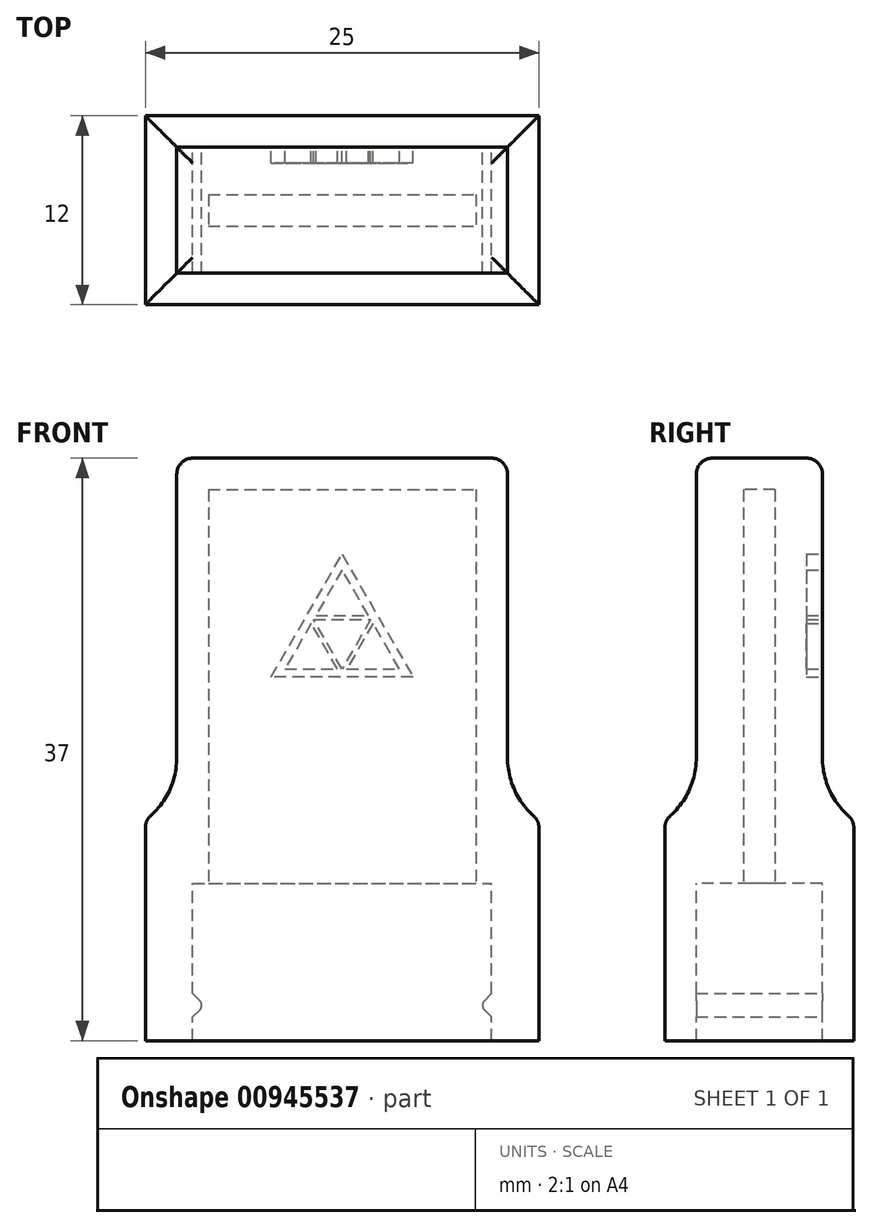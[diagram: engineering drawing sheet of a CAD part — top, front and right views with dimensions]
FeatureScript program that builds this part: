
annotation { "Feature Type Name" : "Feature", "Feature Type Description" : "" }
export const myFeature = defineFeature(function(context is Context, id is Id, definition is map)
    precondition{}
    {
        {
            var Q0;
            Q0=qCreatedBy(makeId("Top.planeOp"),FACE);
            var sketch = newSketch(context, id + "F0", { "sketchPlane" : qUnion([Q0])});
            skLineSegment(sketch, "E0.bottom", {"start": v(0, 0) * mm, "end": v(25, 0) * mm});
            skLineSegment(sketch, "E0.top", {"start": v(0, 12) * mm, "end": v(25, 12) * mm});
            skLineSegment(sketch, "E0.left", {"start": v(0, 0) * mm, "end": v(0, 12) * mm});
            skLineSegment(sketch, "E0.right", {"start": v(25, 0) * mm, "end": v(25, 12) * mm});
            skLineSegment(sketch, "E1.bottom", {"start": v(3, 10) * mm, "end": v(22, 10) * mm});
            skLineSegment(sketch, "E1.top", {"start": v(3, 2) * mm, "end": v(22, 2) * mm});
            skLineSegment(sketch, "E1.left", {"start": v(3, 10) * mm, "end": v(3, 2) * mm});
            skLineSegment(sketch, "E1.right", {"start": v(22, 10) * mm, "end": v(22, 2) * mm});
            skSolve(sketch);
        }
        {
            var Q0;
            Q0=makeQuery(id+"F0.imprint","IMPRINT",FACE,{"disambiguationData":[TD([[makeQuery(id+"F0.imprint","IMPRINT",EDGE,{"derivedFrom":sQuery(id+"F0.wireOp",EDGE,"E0.bottom")}),1.0]])]});
            extrude(context, id + "F1", {"entities" : qUnion([Q0]), "oppositeDirection" : true, "depth" : 10 * mm, "offsetDistance" : 25 * mm});
        }
        {
            var Q0;
            Q0=qCreatedBy(makeId("Top.planeOp"),FACE);
            var sketch = newSketch(context, id + "F2", { "sketchPlane" : qUnion([Q0])});
            skLineSegment(sketch, "E2.bottom", {"start": v(4, 7) * mm, "end": v(21, 7) * mm});
            skLineSegment(sketch, "E2.top", {"start": v(4, 5) * mm, "end": v(21, 5) * mm});
            skLineSegment(sketch, "E2.left", {"start": v(4, 7) * mm, "end": v(4, 5) * mm});
            skLineSegment(sketch, "E2.right", {"start": v(21, 7) * mm, "end": v(21, 5) * mm});
            skLineSegment(sketch, "E3.bottom", {"start": v(2, 10) * mm, "end": v(23, 10) * mm});
            skLineSegment(sketch, "E3.top", {"start": v(2, 2) * mm, "end": v(23, 2) * mm});
            skLineSegment(sketch, "E3.left", {"start": v(2, 10) * mm, "end": v(2, 2) * mm});
            skLineSegment(sketch, "E3.right", {"start": v(23, 10) * mm, "end": v(23, 2) * mm});
            skSolve(sketch);
        }
        {
            var Q0;
            Q0=makeQuery(id+"F2.imprint","IMPRINT",FACE,{"disambiguationData":[TD([[makeQuery(id+"F2.imprint","IMPRINT",EDGE,{"derivedFrom":sQuery(id+"F2.wireOp",EDGE,"E2.bottom")}),1.0]])]});
            extrude(context, id + "F3", {"entities" : qUnion([Q0]), "depth" : 25 * mm, "offsetDistance" : 25 * mm});
        }
        {
            var Q0;
            Q0=makeQuery(id+"F3.opExtrude","CAP_FACE",FACE,{"disambiguationData":[OSD([sQuery(id+"F2.wireOp",EDGE,"E2.bottom"),sQuery(id+"F2.wireOp",EDGE,"E2.top"),sQuery(id+"F2.wireOp",EDGE,"E2.left"),sQuery(id+"F2.wireOp",EDGE,"E2.right"),sQuery(id+"F2.wireOp",EDGE,"E3.bottom"),sQuery(id+"F2.wireOp",EDGE,"E3.top"),sQuery(id+"F2.wireOp",EDGE,"E3.left"),sQuery(id+"F2.wireOp",EDGE,"E3.right")])],"isStart":false});
            var sketch = newSketch(context, id + "F4", { "sketchPlane" : qUnion([Q0])});
            skSolve(sketch);
        }
        {
            var Q0;
            Q0=makeQuery(id+"F4.imprint","IMPRINT",FACE,{"disambiguationData":[TD([[makeQuery(id+"F4.imprint","IMPRINT",EDGE,{"derivedFrom":makeQuery(id+"F3.opExtrude","CAP_EDGE",EDGE,{"disambiguationData":[OSD([sQuery(id+"F2.wireOp",EDGE,"E2.bottom")])],"isStart":false})}),1.0]])]});
            var Q1;
            Q1=makeQuery(id+"F4.imprint","IMPRINT",FACE,{"disambiguationData":[TD([[makeQuery(id+"F4.imprint","IMPRINT",EDGE,{"derivedFrom":makeQuery(id+"F3.opExtrude","CAP_EDGE",EDGE,{"disambiguationData":[OSD([sQuery(id+"F2.wireOp",EDGE,"E2.bottom")])],"isStart":false})}),-1.0]])]});
            extrude(context, id + "F5", {"entities" : qUnion([Q0, Q1]), "operationType" : NewBodyOperationType.ADD, "depth" : 2 * mm, "offsetDistance" : 25 * mm});
        }
        {
            var Q0;
            Q0=makeQuery(id+"F1.opExtrude","CAP_FACE",FACE,{"disambiguationData":[OSD([sQuery(id+"F0.wireOp",EDGE,"E0.bottom"),sQuery(id+"F0.wireOp",EDGE,"E0.top"),sQuery(id+"F0.wireOp",EDGE,"E0.left"),sQuery(id+"F0.wireOp",EDGE,"E0.right"),sQuery(id+"F0.wireOp",EDGE,"E1.bottom"),sQuery(id+"F0.wireOp",EDGE,"E1.top"),sQuery(id+"F0.wireOp",EDGE,"E1.left"),sQuery(id+"F0.wireOp",EDGE,"E1.right")])],"isStart":true});
            var sketch = newSketch(context, id + "F6", { "sketchPlane" : qUnion([Q0])});
            skSolve(sketch);
        }
        {
            var Q0;
            Q0=makeQuery(id+"F6.imprint","IMPRINT",FACE,{"disambiguationData":[TD([[makeQuery(id+"F6.imprint","IMPRINT",EDGE,{"derivedFrom":makeQuery(id+"F1.opExtrude","CAP_EDGE",EDGE,{"disambiguationData":[OSD([sQuery(id+"F0.wireOp",EDGE,"E0.bottom")])],"isStart":true})}),1.0]])]});
            extrude(context, id + "F7", {"entities" : qUnion([Q0]), "operationType" : NewBodyOperationType.ADD, "depth" : 4 * mm, "offsetDistance" : 25 * mm});
        }
        {
            var Q0;
            Q0=qCreatedBy(makeId("Front.planeOp"),FACE);
            cPlane(context, id + "F8", {"entities" : qUnion([Q0]), "cplaneType" : CPlaneType.OFFSET, "offset" : 6 * mm, "oppositeDirection" : true, "width" : 150 * mm, "height" : 150 * mm});
        }
        {
            var Q0;
            Q0=qCreatedBy(id+"F8.planeOp",FACE);
            var sketch = newSketch(context, id + "F9", { "sketchPlane" : qUnion([Q0])});
            skLineSegment(sketch, "E4", {"start": v(0, 0) * mm, "end": v(0, -10) * mm});
            skLineSegment(sketch, "E5", {"start": v(0, -10) * mm, "end": v(3, -10) * mm});
            skLineSegment(sketch, "E6", {"start": v(3, -10) * mm, "end": v(3, -8.5) * mm});
            skLineSegment(sketch, "E7", {"start": v(3, -8.5) * mm, "end": v(3.47, -8.03) * mm});
            skLineSegment(sketch, "E8", {"start": v(3.47, -7.47) * mm, "end": v(3, -7) * mm});
            skLineSegment(sketch, "E9", {"start": v(3, -7) * mm, "end": v(3, -8.5) * mm});
            skPoint(sketch, "E10.visualSharp", {"position": v(3.75, -7.75) * mm});
            skArc(sketch, "E10.filletArc", {"start": v(3.47, -8.03) * mm, "mid": v(3.58, -7.75) * mm, "end": v(3.47, -7.47) * mm});
            skLineSegment(sketch, "E11", {"start": v(22, -8.5) * mm, "end": v(22, -7) * mm});
            skLineSegment(sketch, "E12", {"start": v(22, -7) * mm, "end": v(21.53, -7.47) * mm});
            skLineSegment(sketch, "E13", {"start": v(21.53, -8.03) * mm, "end": v(22, -8.5) * mm});
            skPoint(sketch, "E14.visualSharp", {"position": v(21.25, -7.75) * mm});
            skArc(sketch, "E14.filletArc", {"start": v(21.53, -7.47) * mm, "mid": v(21.42, -7.75) * mm, "end": v(21.53, -8.03) * mm});
            skSolve(sketch);
        }
        {
            var Q0;
            Q0=makeQuery(id+"F9.imprint","IMPRINT",FACE,{"disambiguationData":[TD([[makeQuery(id+"F9.imprint","IMPRINT",EDGE,{"derivedFrom":sQuery(id+"F9.wireOp",EDGE,"E7")}),1.0]])]});
            var Q1;
            Q1=makeQuery(id+"F9.imprint","IMPRINT",FACE,{"disambiguationData":[TD([[makeQuery(id+"F9.imprint","IMPRINT",EDGE,{"derivedFrom":sQuery(id+"F9.wireOp",EDGE,"E11")}),1.0]])]});
            extrude(context, id + "F10", {"entities" : qUnion([Q0, Q1]), "operationType" : NewBodyOperationType.ADD, "endBound" : BoundingType.UP_TO_NEXT, "depth" : 25 * mm, "offsetDistance" : 25 * mm, "hasSecondDirection" : true, "secondDirectionBound" : SecondDirectionBoundingType.UP_TO_NEXT, "secondDirectionOppositeDirection" : true, "secondDirectionDepth" : 25 * mm});
        }
        {
            var Q0;
            {var subQ0=sQuery(id+"F2.wireOp",EDGE,"E3.top");Q0=makeQuery(id+"F7.boolean.opBoolean","INTERSECT",EDGE,{"derivedFrom":[makeQuery(id+"F5.boolean.opBoolean","MERGE",FACE,{"derivedFrom":[makeQuery(id+"F3.opExtrude","SWEPT_FACE",FACE,{"disambiguationData":[OSD([subQ0])]}),makeQuery(id+"F5.opExtrude","SWEPT_FACE",FACE,{"disambiguationData":[OSD([subQ0])]})]}),makeQuery(id+"F7.opExtrude","CAP_FACE",FACE,{"disambiguationData":[OSD([sQuery(id+"F0.wireOp",EDGE,"E0.bottom"),sQuery(id+"F0.wireOp",EDGE,"E0.top"),sQuery(id+"F0.wireOp",EDGE,"E0.left"),sQuery(id+"F0.wireOp",EDGE,"E0.right"),sQuery(id+"F0.wireOp",EDGE,"E1.bottom"),sQuery(id+"F0.wireOp",EDGE,"E1.top"),sQuery(id+"F0.wireOp",EDGE,"E1.left"),sQuery(id+"F0.wireOp",EDGE,"E1.right")])],"isStart":false})]});}
            var Q1;
            {var subQ0=sQuery(id+"F2.wireOp",EDGE,"E3.right");Q1=makeQuery(id+"F7.boolean.opBoolean","INTERSECT",EDGE,{"derivedFrom":[makeQuery(id+"F5.boolean.opBoolean","MERGE",FACE,{"derivedFrom":[makeQuery(id+"F3.opExtrude","SWEPT_FACE",FACE,{"disambiguationData":[OSD([subQ0])]}),makeQuery(id+"F5.opExtrude","SWEPT_FACE",FACE,{"disambiguationData":[OSD([subQ0])]})]}),makeQuery(id+"F7.opExtrude","CAP_FACE",FACE,{"disambiguationData":[OSD([sQuery(id+"F0.wireOp",EDGE,"E0.bottom"),sQuery(id+"F0.wireOp",EDGE,"E0.top"),sQuery(id+"F0.wireOp",EDGE,"E0.left"),sQuery(id+"F0.wireOp",EDGE,"E0.right"),sQuery(id+"F0.wireOp",EDGE,"E1.bottom"),sQuery(id+"F0.wireOp",EDGE,"E1.top"),sQuery(id+"F0.wireOp",EDGE,"E1.left"),sQuery(id+"F0.wireOp",EDGE,"E1.right")])],"isStart":false})]});}
            var Q2;
            {var subQ0=sQuery(id+"F2.wireOp",EDGE,"E3.bottom");Q2=makeQuery(id+"F7.boolean.opBoolean","INTERSECT",EDGE,{"derivedFrom":[makeQuery(id+"F5.boolean.opBoolean","MERGE",FACE,{"derivedFrom":[makeQuery(id+"F3.opExtrude","SWEPT_FACE",FACE,{"disambiguationData":[OSD([subQ0])]}),makeQuery(id+"F5.opExtrude","SWEPT_FACE",FACE,{"disambiguationData":[OSD([subQ0])]})]}),makeQuery(id+"F7.opExtrude","CAP_FACE",FACE,{"disambiguationData":[OSD([sQuery(id+"F0.wireOp",EDGE,"E0.bottom"),sQuery(id+"F0.wireOp",EDGE,"E0.top"),sQuery(id+"F0.wireOp",EDGE,"E0.left"),sQuery(id+"F0.wireOp",EDGE,"E0.right"),sQuery(id+"F0.wireOp",EDGE,"E1.bottom"),sQuery(id+"F0.wireOp",EDGE,"E1.top"),sQuery(id+"F0.wireOp",EDGE,"E1.left"),sQuery(id+"F0.wireOp",EDGE,"E1.right")])],"isStart":false})]});}
            var Q3;
            {var subQ0=sQuery(id+"F2.wireOp",EDGE,"E3.left");Q3=makeQuery(id+"F7.boolean.opBoolean","INTERSECT",EDGE,{"derivedFrom":[makeQuery(id+"F5.boolean.opBoolean","MERGE",FACE,{"derivedFrom":[makeQuery(id+"F3.opExtrude","SWEPT_FACE",FACE,{"disambiguationData":[OSD([subQ0])]}),makeQuery(id+"F5.opExtrude","SWEPT_FACE",FACE,{"disambiguationData":[OSD([subQ0])]})]}),makeQuery(id+"F7.opExtrude","CAP_FACE",FACE,{"disambiguationData":[OSD([sQuery(id+"F0.wireOp",EDGE,"E0.bottom"),sQuery(id+"F0.wireOp",EDGE,"E0.top"),sQuery(id+"F0.wireOp",EDGE,"E0.left"),sQuery(id+"F0.wireOp",EDGE,"E0.right"),sQuery(id+"F0.wireOp",EDGE,"E1.bottom"),sQuery(id+"F0.wireOp",EDGE,"E1.top"),sQuery(id+"F0.wireOp",EDGE,"E1.left"),sQuery(id+"F0.wireOp",EDGE,"E1.right")])],"isStart":false})]});}
            fillet(context, id + "F11", {"entities" : qUnion([Q0, Q1, Q2, Q3]), "radius" : 5 * mm, "tangentPropagation" : true, "allowEdgeOverflow" : false});
        }
        {
            var Q0;
            Q0=makeQuery(id+"F5.opExtrude","CAP_EDGE",EDGE,{"disambiguationData":[OSD([sQuery(id+"F2.wireOp",EDGE,"E3.right")])],"isStart":false});
            var Q1;
            Q1=makeQuery(id+"F5.opExtrude","CAP_EDGE",EDGE,{"disambiguationData":[OSD([sQuery(id+"F2.wireOp",EDGE,"E3.top")])],"isStart":false});
            var Q2;
            Q2=makeQuery(id+"F5.opExtrude","CAP_EDGE",EDGE,{"disambiguationData":[OSD([sQuery(id+"F2.wireOp",EDGE,"E3.left")])],"isStart":false});
            var Q3;
            Q3=makeQuery(id+"F5.opExtrude","CAP_EDGE",EDGE,{"disambiguationData":[OSD([sQuery(id+"F2.wireOp",EDGE,"E3.bottom")])],"isStart":false});
            var Q4;
            {var subQ0=sQuery(id+"F0.wireOp",EDGE,"E0.top");var subQ1=sQuery(id+"F2.wireOp",EDGE,"E3.bottom");Q4=makeQuery(id+"F11.opFillet","BLEND_EDGE",EDGE,{"blendedFrom":[makeQuery(id+"F7.boolean.opBoolean","INTERSECT",EDGE,{"derivedFrom":[makeQuery(id+"F5.boolean.opBoolean","MERGE",FACE,{"derivedFrom":[makeQuery(id+"F3.opExtrude","SWEPT_FACE",FACE,{"disambiguationData":[OSD([subQ1])]}),makeQuery(id+"F5.opExtrude","SWEPT_FACE",FACE,{"disambiguationData":[OSD([subQ1])]})]}),makeQuery(id+"F7.opExtrude","CAP_FACE",FACE,{"disambiguationData":[OSD([sQuery(id+"F0.wireOp",EDGE,"E0.bottom"),subQ0,sQuery(id+"F0.wireOp",EDGE,"E0.left"),sQuery(id+"F0.wireOp",EDGE,"E0.right"),sQuery(id+"F0.wireOp",EDGE,"E1.bottom"),sQuery(id+"F0.wireOp",EDGE,"E1.top"),sQuery(id+"F0.wireOp",EDGE,"E1.left"),sQuery(id+"F0.wireOp",EDGE,"E1.right")])],"isStart":false})]}),makeQuery(id+"F7.boolean.opBoolean","MERGE",FACE,{"derivedFrom":[makeQuery(id+"F1.opExtrude","SWEPT_FACE",FACE,{"disambiguationData":[OSD([subQ0])]}),makeQuery(id+"F7.opExtrude","SWEPT_FACE",FACE,{"disambiguationData":[OSD([subQ0])]})]})],"blendedInto":[makeQuery(id+"F7.boolean.opBoolean","MERGE",FACE,{"derivedFrom":[makeQuery(id+"F1.opExtrude","SWEPT_FACE",FACE,{"disambiguationData":[OSD([subQ0])]}),makeQuery(id+"F7.opExtrude","SWEPT_FACE",FACE,{"disambiguationData":[OSD([subQ0])]})]})]});}
            var Q5;
            {var subQ0=sQuery(id+"F0.wireOp",EDGE,"E0.right");var subQ1=sQuery(id+"F2.wireOp",EDGE,"E3.right");Q5=makeQuery(id+"F11.opFillet","BLEND_EDGE",EDGE,{"blendedFrom":[makeQuery(id+"F7.boolean.opBoolean","INTERSECT",EDGE,{"derivedFrom":[makeQuery(id+"F5.boolean.opBoolean","MERGE",FACE,{"derivedFrom":[makeQuery(id+"F3.opExtrude","SWEPT_FACE",FACE,{"disambiguationData":[OSD([subQ1])]}),makeQuery(id+"F5.opExtrude","SWEPT_FACE",FACE,{"disambiguationData":[OSD([subQ1])]})]}),makeQuery(id+"F7.opExtrude","CAP_FACE",FACE,{"disambiguationData":[OSD([sQuery(id+"F0.wireOp",EDGE,"E0.bottom"),sQuery(id+"F0.wireOp",EDGE,"E0.top"),sQuery(id+"F0.wireOp",EDGE,"E0.left"),subQ0,sQuery(id+"F0.wireOp",EDGE,"E1.bottom"),sQuery(id+"F0.wireOp",EDGE,"E1.top"),sQuery(id+"F0.wireOp",EDGE,"E1.left"),sQuery(id+"F0.wireOp",EDGE,"E1.right")])],"isStart":false})]}),makeQuery(id+"F7.boolean.opBoolean","MERGE",FACE,{"derivedFrom":[makeQuery(id+"F1.opExtrude","SWEPT_FACE",FACE,{"disambiguationData":[OSD([subQ0])]}),makeQuery(id+"F7.opExtrude","SWEPT_FACE",FACE,{"disambiguationData":[OSD([subQ0])]})]})],"blendedInto":[makeQuery(id+"F7.boolean.opBoolean","MERGE",FACE,{"derivedFrom":[makeQuery(id+"F1.opExtrude","SWEPT_FACE",FACE,{"disambiguationData":[OSD([subQ0])]}),makeQuery(id+"F7.opExtrude","SWEPT_FACE",FACE,{"disambiguationData":[OSD([subQ0])]})]})]});}
            var Q6;
            {var subQ0=sQuery(id+"F0.wireOp",EDGE,"E0.bottom");var subQ1=sQuery(id+"F2.wireOp",EDGE,"E3.top");Q6=makeQuery(id+"F11.opFillet","BLEND_EDGE",EDGE,{"blendedFrom":[makeQuery(id+"F7.boolean.opBoolean","INTERSECT",EDGE,{"derivedFrom":[makeQuery(id+"F5.boolean.opBoolean","MERGE",FACE,{"derivedFrom":[makeQuery(id+"F3.opExtrude","SWEPT_FACE",FACE,{"disambiguationData":[OSD([subQ1])]}),makeQuery(id+"F5.opExtrude","SWEPT_FACE",FACE,{"disambiguationData":[OSD([subQ1])]})]}),makeQuery(id+"F7.opExtrude","CAP_FACE",FACE,{"disambiguationData":[OSD([subQ0,sQuery(id+"F0.wireOp",EDGE,"E0.top"),sQuery(id+"F0.wireOp",EDGE,"E0.left"),sQuery(id+"F0.wireOp",EDGE,"E0.right"),sQuery(id+"F0.wireOp",EDGE,"E1.bottom"),sQuery(id+"F0.wireOp",EDGE,"E1.top"),sQuery(id+"F0.wireOp",EDGE,"E1.left"),sQuery(id+"F0.wireOp",EDGE,"E1.right")])],"isStart":false})]}),makeQuery(id+"F7.boolean.opBoolean","MERGE",FACE,{"derivedFrom":[makeQuery(id+"F1.opExtrude","SWEPT_FACE",FACE,{"disambiguationData":[OSD([subQ0])]}),makeQuery(id+"F7.opExtrude","SWEPT_FACE",FACE,{"disambiguationData":[OSD([subQ0])]})]})],"blendedInto":[makeQuery(id+"F7.boolean.opBoolean","MERGE",FACE,{"derivedFrom":[makeQuery(id+"F1.opExtrude","SWEPT_FACE",FACE,{"disambiguationData":[OSD([subQ0])]}),makeQuery(id+"F7.opExtrude","SWEPT_FACE",FACE,{"disambiguationData":[OSD([subQ0])]})]})]});}
            var Q7;
            {var subQ0=sQuery(id+"F0.wireOp",EDGE,"E0.left");var subQ1=sQuery(id+"F2.wireOp",EDGE,"E3.left");Q7=makeQuery(id+"F11.opFillet","BLEND_EDGE",EDGE,{"blendedFrom":[makeQuery(id+"F7.boolean.opBoolean","INTERSECT",EDGE,{"derivedFrom":[makeQuery(id+"F5.boolean.opBoolean","MERGE",FACE,{"derivedFrom":[makeQuery(id+"F3.opExtrude","SWEPT_FACE",FACE,{"disambiguationData":[OSD([subQ1])]}),makeQuery(id+"F5.opExtrude","SWEPT_FACE",FACE,{"disambiguationData":[OSD([subQ1])]})]}),makeQuery(id+"F7.opExtrude","CAP_FACE",FACE,{"disambiguationData":[OSD([sQuery(id+"F0.wireOp",EDGE,"E0.bottom"),sQuery(id+"F0.wireOp",EDGE,"E0.top"),subQ0,sQuery(id+"F0.wireOp",EDGE,"E0.right"),sQuery(id+"F0.wireOp",EDGE,"E1.bottom"),sQuery(id+"F0.wireOp",EDGE,"E1.top"),sQuery(id+"F0.wireOp",EDGE,"E1.left"),sQuery(id+"F0.wireOp",EDGE,"E1.right")])],"isStart":false})]}),makeQuery(id+"F7.boolean.opBoolean","MERGE",FACE,{"derivedFrom":[makeQuery(id+"F1.opExtrude","SWEPT_FACE",FACE,{"disambiguationData":[OSD([subQ0])]}),makeQuery(id+"F7.opExtrude","SWEPT_FACE",FACE,{"disambiguationData":[OSD([subQ0])]})]})],"blendedInto":[makeQuery(id+"F7.boolean.opBoolean","MERGE",FACE,{"derivedFrom":[makeQuery(id+"F1.opExtrude","SWEPT_FACE",FACE,{"disambiguationData":[OSD([subQ0])]}),makeQuery(id+"F7.opExtrude","SWEPT_FACE",FACE,{"disambiguationData":[OSD([subQ0])]})]})]});}
            fillet(context, id + "F12", {"entities" : qUnion([Q0, Q1, Q2, Q3, Q4, Q5, Q6, Q7]), "radius" : 1 * mm, "tangentPropagation" : true, "allowEdgeOverflow" : false});
        }
        {
            var Q0;
            {var subQ0=sQuery(id+"F2.wireOp",EDGE,"E3.bottom");Q0=makeQuery(id+"F5.boolean.opBoolean","MERGE",FACE,{"derivedFrom":[makeQuery(id+"F3.opExtrude","SWEPT_FACE",FACE,{"disambiguationData":[OSD([subQ0])]}),makeQuery(id+"F5.opExtrude","SWEPT_FACE",FACE,{"disambiguationData":[OSD([subQ0])]})]});}
            var sketch = newSketch(context, id + "F13", { "sketchPlane" : qUnion([Q0])});
            skLineSegment(sketch, "E15", {"start": v(-17, 13.1) * mm, "end": v(-8, 13.1) * mm});
            skLineSegment(sketch, "E16", {"start": v(-8, 13.1) * mm, "end": v(-12.5, 20.9) * mm});
            skLineSegment(sketch, "E17", {"start": v(-12.5, 20.9) * mm, "end": v(-17, 13.1) * mm});
            skLineSegment(sketch, "E18", {"start": v(-14.46, 16.5) * mm, "end": v(-12.79, 13.6) * mm});
            skLineSegment(sketch, "E19", {"start": v(-12.21, 13.6) * mm, "end": v(-10.54, 16.5) * mm});
            skLineSegment(sketch, "E20", {"start": v(-10.83, 17) * mm, "end": v(-14.17, 17) * mm});
            skLineSegment(sketch, "E21", {"start": v(-16.13, 13.6) * mm, "end": v(-14.46, 16.5) * mm});
            skLineSegment(sketch, "E22", {"start": v(-12.5, 19.9) * mm, "end": v(-10.83, 17) * mm});
            skLineSegment(sketch, "E23", {"start": v(-8.87, 13.6) * mm, "end": v(-12.21, 13.6) * mm});
            skPoint(sketch, "E24.orphan", {"position": v(-16.18, 13.53) * mm});
            skPoint(sketch, "E25.orphan", {"position": v(-16.18, 13.6) * mm});
            skLineSegment(sketch, "E26", {"start": v(-14.32, 16.75) * mm, "end": v(-12.5, 13.6) * mm});
            skLineSegment(sketch, "E27", {"start": v(-12.5, 13.6) * mm, "end": v(-10.68, 16.75) * mm});
            skLineSegment(sketch, "E28", {"start": v(-10.68, 16.75) * mm, "end": v(-14.32, 16.75) * mm});
            skPoint(sketch, "E29.orphan", {"position": v(-14.75, 17) * mm});
            skLineSegment(sketch, "E30.trimOffspring", {"start": v(-14.17, 17) * mm, "end": v(-12.5, 19.9) * mm});
            skLineSegment(sketch, "E31.trimOffspring", {"start": v(-12.79, 13.6) * mm, "end": v(-16.13, 13.6) * mm});
            skPoint(sketch, "E32.orphan", {"position": v(-12.5, 13.1) * mm});
            skLineSegment(sketch, "E33.trimOffspring", {"start": v(-10.54, 16.5) * mm, "end": v(-8.87, 13.6) * mm});
            skPoint(sketch, "E34.orphan", {"position": v(-10.25, 17) * mm});
            skSolve(sketch);
        }
        {
            var Q0;
            Q0=makeQuery(id+"F13.imprint","IMPRINT",FACE,{"disambiguationData":[TD([[makeQuery(id+"F13.imprint","IMPRINT",EDGE,{"derivedFrom":sQuery(id+"F13.wireOp",EDGE,"E15")}),1.0]])]});
            extrude(context, id + "F14", {"entities" : qUnion([Q0]), "operationType" : NewBodyOperationType.REMOVE, "oppositeDirection" : true, "depth" : 1 * mm, "offsetDistance" : 25 * mm});
        }
    });
